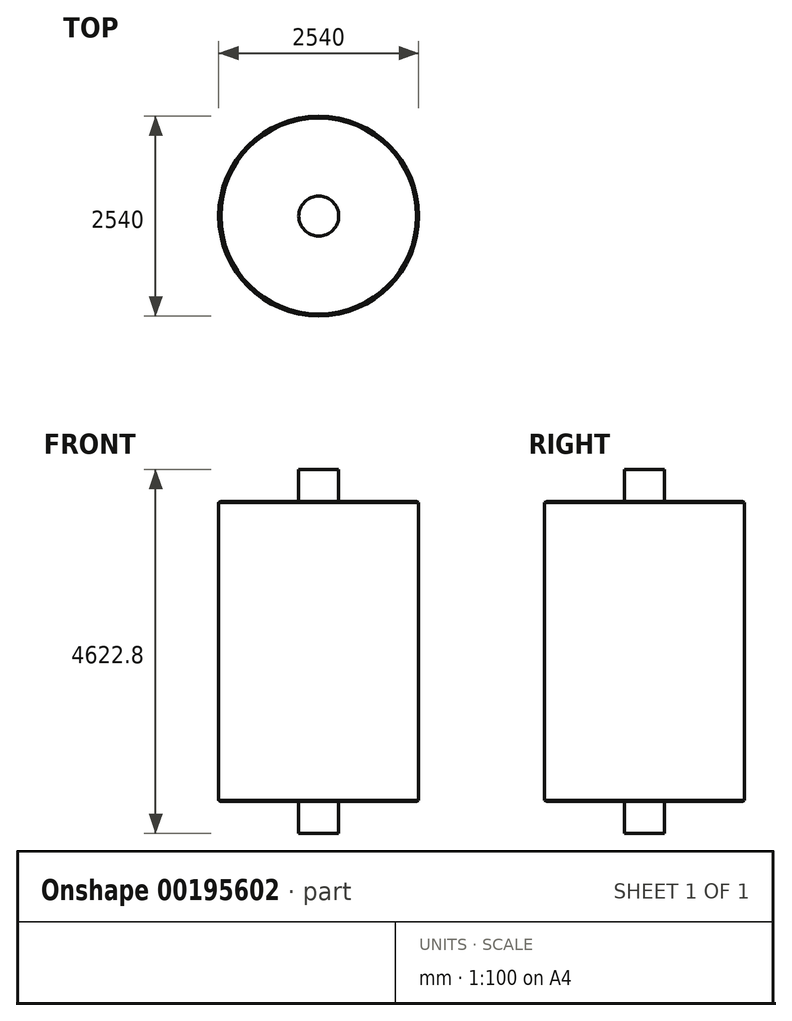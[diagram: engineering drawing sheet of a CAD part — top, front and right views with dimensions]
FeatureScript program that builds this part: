
annotation { "Feature Type Name" : "Feature", "Feature Type Description" : "" }
export const myFeature = defineFeature(function(context is Context, id is Id, definition is map)
    precondition{}
    {
        {
            var Q0;
            Q0=qCreatedBy(makeId("Front.planeOp"),FACE);
            var sketch = newSketch(context, id + "F0", { "sketchPlane" : qUnion([Q0])});
            skLineSegment(sketch, "E0", {"start": v(0, 3810) * mm, "end": v(0, 0) * mm});
            skLineSegment(sketch, "E1", {"start": v(-254, 0) * mm, "end": v(-1270, 0) * mm});
            skLineSegment(sketch, "E2", {"start": v(-1270, 0) * mm, "end": v(-1270, 3810) * mm});
            skLineSegment(sketch, "E3", {"start": v(-1270, 3810) * mm, "end": v(-254, 3810) * mm});
            skLineSegment(sketch, "E4", {"start": v(0, 3810) * mm, "end": v(0, 4216.4) * mm});
            skLineSegment(sketch, "E5", {"start": v(0, 4216.4) * mm, "end": v(-254, 4216.4) * mm});
            skLineSegment(sketch, "E6", {"start": v(-254, 4216.4) * mm, "end": v(-254, 3810) * mm});
            skLineSegment(sketch, "E7", {"start": v(0, 0) * mm, "end": v(0, -406.4) * mm});
            skLineSegment(sketch, "E8", {"start": v(0, -406.4) * mm, "end": v(-254, -406.4) * mm});
            skLineSegment(sketch, "E9", {"start": v(-254, -406.4) * mm, "end": v(-254, 0) * mm});
            skSolve(sketch);
        }
        {
            var Q0;
            Q0=sQuery(id+"F0.wireOp",EDGE,"E2");
            var Q1;
            Q1=sQuery(id+"F0.wireOp",EDGE,"E1");
            var Q2;
            Q2=sQuery(id+"F0.wireOp",EDGE,"E3");
            var Q3;
            Q3=sQuery(id+"F0.wireOp",EDGE,"E8");
            var Q4;
            Q4=sQuery(id+"F0.wireOp",EDGE,"E9");
            var Q5;
            Q5=sQuery(id+"F0.wireOp",EDGE,"E6");
            var Q6;
            Q6=sQuery(id+"F0.wireOp",EDGE,"E5");
            var Q7;
            Q7=sQuery(id+"F0.wireOp",EDGE,"E0");
            revolve(context, id + "F1", {"bodyType" : ToolBodyType.SURFACE, "surfaceEntities" : qUnion([Q0, Q1, Q2, Q3, Q4, Q5, Q6]), "axis" : qUnion([Q7]), "revolveType" : RevolveType.FULL});
        }
        {
            var Q0;
            Q0=makeQuery(id+"F1.opRevolve","SWEPT_EDGE",EDGE,{"disambiguationData":[OSD([sQuery(id+"F0.wireOp",VERTEX,"E3.start")])]});
            var Q1;
            Q1=makeQuery(id+"F1.opRevolve","SWEPT_EDGE",EDGE,{"disambiguationData":[OSD([sQuery(id+"F0.wireOp",VERTEX,"E1.end")])]});
            chamfer(context, id + "F2", {"entities" : qUnion([Q0, Q1]), "width" : 5.08 * mm, "tangentPropagation" : true});
        }
        {
            var Q0;
            Q0=makeQuery(id+"F2.opChamfer","BLEND_EDGE",EDGE,{"blendedFrom":[makeQuery(id+"F1.opRevolve","SWEPT_EDGE",EDGE,{"disambiguationData":[OSD([sQuery(id+"F0.wireOp",VERTEX,"E3.start")])]}),makeQuery(id+"F1.opRevolve","SWEPT_FACE",FACE,{"disambiguationData":[OSD([sQuery(id+"F0.wireOp",EDGE,"E3")])]})],"blendedInto":[makeQuery(id+"F1.opRevolve","SWEPT_FACE",FACE,{"disambiguationData":[OSD([sQuery(id+"F0.wireOp",EDGE,"E3")])]})]});
            var Q1;
            Q1=makeQuery(id+"F2.opChamfer","BLEND_EDGE",EDGE,{"blendedFrom":[makeQuery(id+"F1.opRevolve","SWEPT_EDGE",EDGE,{"disambiguationData":[OSD([sQuery(id+"F0.wireOp",VERTEX,"E1.end")])]}),makeQuery(id+"F1.opRevolve","SWEPT_FACE",FACE,{"disambiguationData":[OSD([sQuery(id+"F0.wireOp",EDGE,"E1")])]})],"blendedInto":[makeQuery(id+"F1.opRevolve","SWEPT_FACE",FACE,{"disambiguationData":[OSD([sQuery(id+"F0.wireOp",EDGE,"E1")])]})]});
            chamfer(context, id + "F3", {"entities" : qUnion([Q0, Q1]), "width" : 50.8 * mm, "tangentPropagation" : true});
        }
    });
